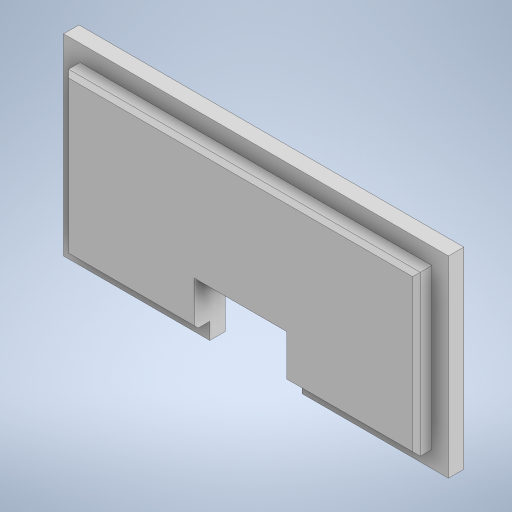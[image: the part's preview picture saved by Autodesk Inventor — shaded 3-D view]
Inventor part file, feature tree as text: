
AUTODESK INVENTOR PART (.ipt)
format: ipt  version: 2024.2 (Build 282272000, 272)  size: 241,152 bytes
history: native  units: mm
features: extrude x3, sketch x3, chamfer x1
ambient origin geometry x8: Origin, YZ Plane, XZ Plane, XY Plane, X Axis, Y Axis, Z Axis, Center Point
bodies: Solid1 (feature_tree)
feature tree (7):
  extrude  "Extrusion1"  Depth=25.0mm
  extrude  "Extrusion2"  Depth=45.7mm
  extrude  "Extrusion3"  Depth=2.15mm
  chamfer  "Chamfer1"  Distance=2.15mm
  sketch  "Sketch1"  dims[d0=50.0mm d1=25.0mm]
  sketch  "Sketch2"  dims[d2=2.0mm d3=0.0mm d4=45.7mm]
  sketch  "Sketch3"  dims[d5=20.7mm d6=2.15mm d7=2.15mm d8=2.0mm d9=0.0mm d10=12.0mm d11=8.0mm d12=19.0mm d13=0.0mm d14=0.0mm d15=0.5mm d16=2.0mm d17=45.0deg]
